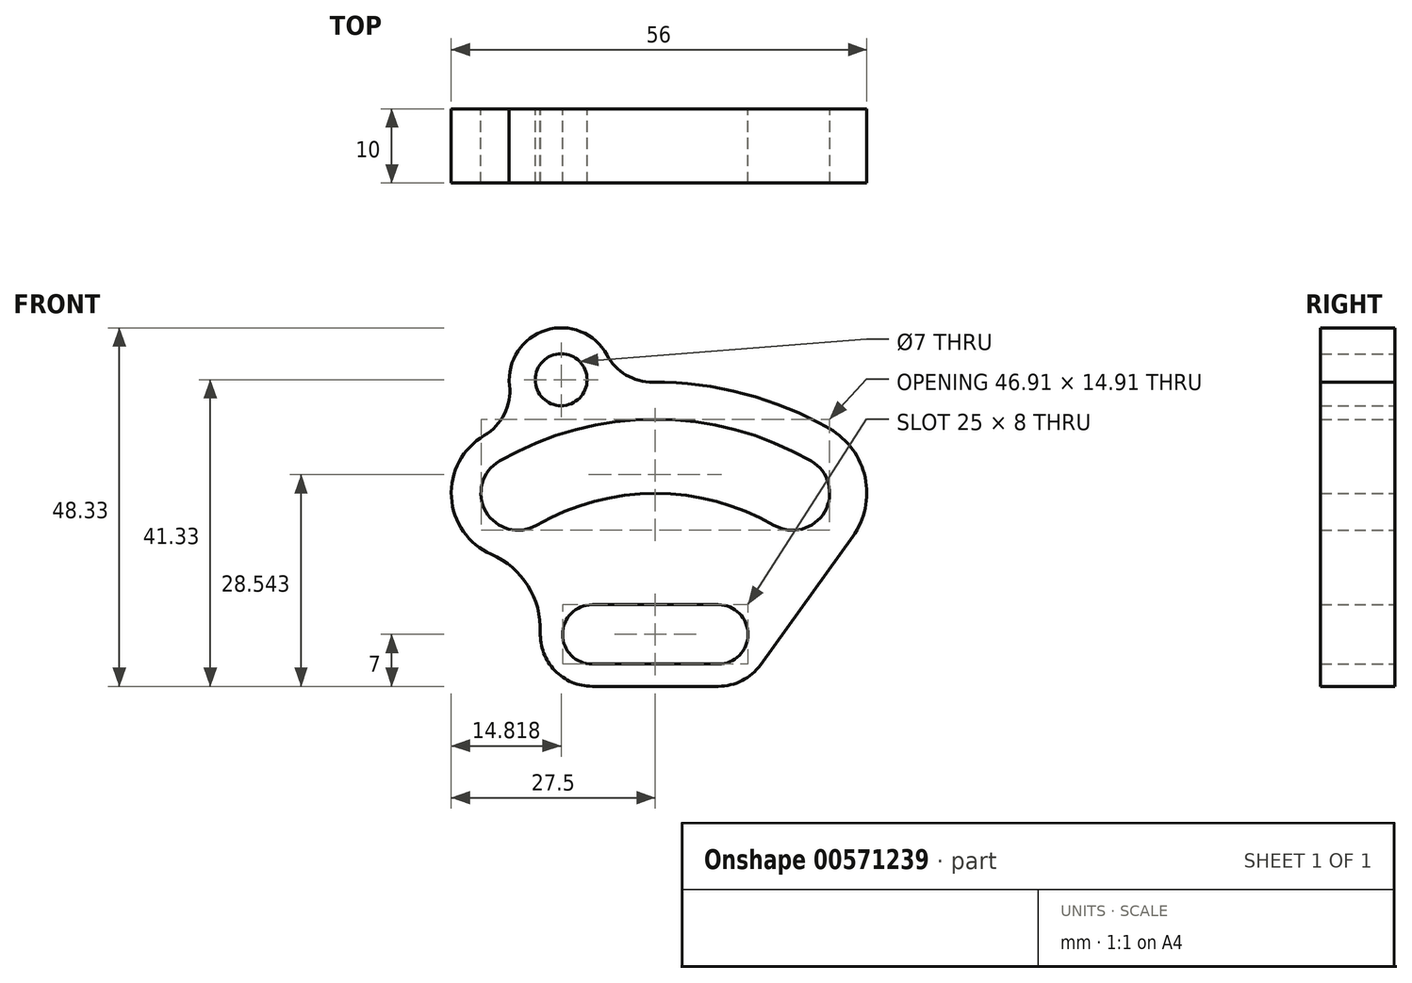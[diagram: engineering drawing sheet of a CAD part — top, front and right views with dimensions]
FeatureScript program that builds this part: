
annotation { "Feature Type Name" : "Feature", "Feature Type Description" : "" }
export const myFeature = defineFeature(function(context is Context, id is Id, definition is map)
    precondition{}
    {
        {
            var Q0;
            Q0=qCreatedBy(makeId("Front.planeOp"),FACE);
            var sketch = newSketch(context, id + "F0", { "sketchPlane" : qUnion([Q0])});
            skCircle(sketch, "E0", {"center": v(0, 0) * mm, "radius": 49 * mm, "construction": true});
            skArc(sketch, "E1", {"start": v(23.5, 40.7) * mm, "mid": v(12, 45.44) * mm, "end": v(-0.32, 47) * mm});
            skArc(sketch, "E2", {"start": v(22.65, 29.26) * mm, "mid": v(0, 37) * mm, "end": v(-22.65, 29.26) * mm, "construction": true});
            skLineSegment(sketch, "E3", {"start": v(0, 0) * mm, "end": v(-14.81, 55.28) * mm, "construction": true});
            skCircle(sketch, "E4", {"center": v(-12.68, 47.33) * mm, "radius": 3.5 * mm});
            skArc(sketch, "E5", {"start": v(-6.53, 50.66) * mm, "mid": v(-14.76, 54.01) * mm, "end": v(-19.64, 46.59) * mm});
            skLineSegment(sketch, "E6", {"start": v(0, 0) * mm, "end": v(-28.97, 50.17) * mm, "construction": true});
            skLineSegment(sketch, "E7", {"start": v(0, 0) * mm, "end": v(28.73, 49.75) * mm, "construction": true});
            skLineSegment(sketch, "E8", {"start": v(28.73, 49.75) * mm, "end": v(27.86, 48.26) * mm});
            skArc(sketch, "E9", {"start": v(16, 27.71) * mm, "mid": v(22.83, 29.54) * mm, "end": v(21, 36.37) * mm});
            skArc(sketch, "E10", {"start": v(-21, 36.37) * mm, "mid": v(-22.83, 29.54) * mm, "end": v(-16, 27.71) * mm});
            skArc(sketch, "E11", {"start": v(21, 36.37) * mm, "mid": v(0, 42) * mm, "end": v(-21, 36.37) * mm});
            skArc(sketch, "E12", {"start": v(16, 27.71) * mm, "mid": v(0, 32) * mm, "end": v(-16, 27.71) * mm});
            skArc(sketch, "E13", {"start": v(26.62, 26.2) * mm, "mid": v(28.28, 34.15) * mm, "end": v(23.5, 40.7) * mm});
            skArc(sketch, "E14", {"start": v(-23, 39.84) * mm, "mid": v(-27.49, 31.54) * mm, "end": v(-22.1, 23.8) * mm});
            skArc(sketch, "E15", {"start": v(-6.53, 50.66) * mm, "mid": v(-3.93, 47.97) * mm, "end": v(-0.32, 47) * mm});
            skArc(sketch, "E16", {"start": v(-23.06, 39.8) * mm, "mid": v(-20.35, 42.7) * mm, "end": v(-19.64, 46.59) * mm});
            skArc(sketch, "E17", {"start": v(8.5, 9) * mm, "mid": v(12.5, 13) * mm, "end": v(8.5, 17) * mm});
            skArc(sketch, "E18", {"start": v(-8.5, 17) * mm, "mid": v(-12.5, 13) * mm, "end": v(-8.5, 9) * mm});
            skLineSegment(sketch, "E19", {"start": v(-8.5, 17) * mm, "end": v(8.5, 17) * mm});
            skLineSegment(sketch, "E20", {"start": v(-8.5, 9) * mm, "end": v(8.5, 9) * mm});
            skArc(sketch, "E21", {"start": v(-15.5, 13.27) * mm, "mid": v(-13.55, 8.15) * mm, "end": v(-8.5, 6) * mm});
            skArc(sketch, "E22", {"start": v(-15.5, 13.27) * mm, "mid": v(-17.17, 19.55) * mm, "end": v(-22.1, 23.8) * mm});
            skArc(sketch, "E23", {"start": v(8.5, 6) * mm, "mid": v(11.7, 6.77) * mm, "end": v(14.18, 8.91) * mm});
            skLineSegment(sketch, "E24", {"start": v(-8.5, 6) * mm, "end": v(8.5, 6) * mm});
            skLineSegment(sketch, "E25", {"start": v(14.18, 8.91) * mm, "end": v(26.62, 26.2) * mm});
            skArc(sketch, "E26.trimOffspring", {"start": v(-2.76, 9) * mm, "mid": v(-2.63, 9.19) * mm, "end": v(-2.51, 9.37) * mm});
            skSolve(sketch);
        }
        {
            var Q0;
            Q0=makeQuery(id+"F0.imprint","IMPRINT",FACE,{"disambiguationData":[TD([[makeQuery(id+"F0.imprint","IMPRINT",EDGE,{"derivedFrom":sQuery(id+"F0.wireOp",EDGE,"E1")}),1.0]])]});
            extrude(context, id + "F1", {"entities" : qUnion([Q0]), "depth" : 10 * mm, "offsetDistance" : 25 * mm});
        }
    });
